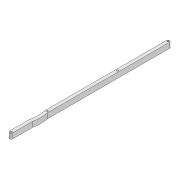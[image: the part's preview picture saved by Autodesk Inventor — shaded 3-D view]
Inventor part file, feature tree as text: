
AUTODESK INVENTOR PART (.ipt)
format: ipt  version: 2022 (Build 260153000, 153)  size: 102,400 bytes
history: native  units: mm
features: extrude x1, other x1, sketch x1
ambient origin geometry x8: Origin, YZ Plane, XZ Plane, XY Plane, X Axis, Y Axis, Z Axis, Center Point
bodies: Solid1 (feature_tree)
feature tree (3):
  extrude  "Extrusion1"  Depth=296.686mm
  other  "Work Axis1"
  sketch  "Sketch1"  dims[d0=6.0mm d1=296.686mm d2=3.0mm d3=3.0mm d4=10.0mm d5=0.0mm d6=3.0mm d7=200.914mm d8=3.0mm d9=68.172mm d10=60.0mm d11=3.0mm d12=30.0mm d13=60.0mm]
